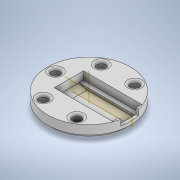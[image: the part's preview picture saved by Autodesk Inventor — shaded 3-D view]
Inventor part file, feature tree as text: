
AUTODESK INVENTOR PART (.ipt)
format: ipt  version: 2021 (Build 250183000, 183)  size: 408,064 bytes
history: native  units: in
note: dims shown in document units (in); Inventor stores cm internally (conversion verified against a paired STEP export)
features: extrude x5, sketch x5, chamfer x2, other x1, plane x1, fillet x1, pattern_circular x1
ambient origin geometry x8: Origin, YZ Plane, XZ Plane, XY Plane, X Axis, Y Axis, Z Axis, Center Point
bodies: Solid1 (feature_tree)
feature tree (16):
  extrude  "Extrusion1"  Depth=0.2992in TaperAngle=0.0deg
  chamfer  "Chamfer2"  Distance=0.1969in
  extrude  "Extrusion2"  TaperAngle=0.0deg  [1 undecoded]
  extrude  "Extrusion3"  Depth=0.1417in
  other  "Work Axis1"
  plane  "Work Plane1"
  extrude  "Extrusion5"  TaperAngle=0.0deg  [1 undecoded]
  extrude  "Extrusion4"  Depth=0.1969in
  fillet  "Fillet4"  Radius=0.2047in
  pattern_circular  "Circular Pattern2"  [2 undecoded]
  chamfer  "Chamfer3"  Distance=0.3618in
  sketch  "Sketch1"  dims[d0=2.0472in d3=0.2992in d4=0.0in]
  sketch  "Sketch2"  dims[d5=1.4394in]
  sketch  "Sketch3"  dims[d6=0.7236in]
  sketch  "Sketch4"  dims[d7=0.3618in]
  sketch  "Sketch7"  dims[d8=0.4961in d9=0.1969in d10=0.0in d11=0.0in d14=0.1417in d15=0.0in d16=0.0in d17=0.2205in d18=0.2047in d19=0.0in d23=0.8268in d24=0.3618in d28=0.5in d29=1.4in d30=0.25in d31=0.0in d32=0.063in d33=0.0in d44=0.1417in d47=0.0551in d48=0.0in d49=0.0in d51=0.0in d54=0.0787in d55=0.0in d56=45.0deg d58=0.063in d59=0.1181in d60=1.9685in d61=240.0deg d63=0.0591in d64=0.1969in d65=45.0deg]
note: 4 required parameter values undecoded (feature->parameter linkage not recoverable at this tier; creation-order binding heuristic only, values carry confidence <= 0.55)
